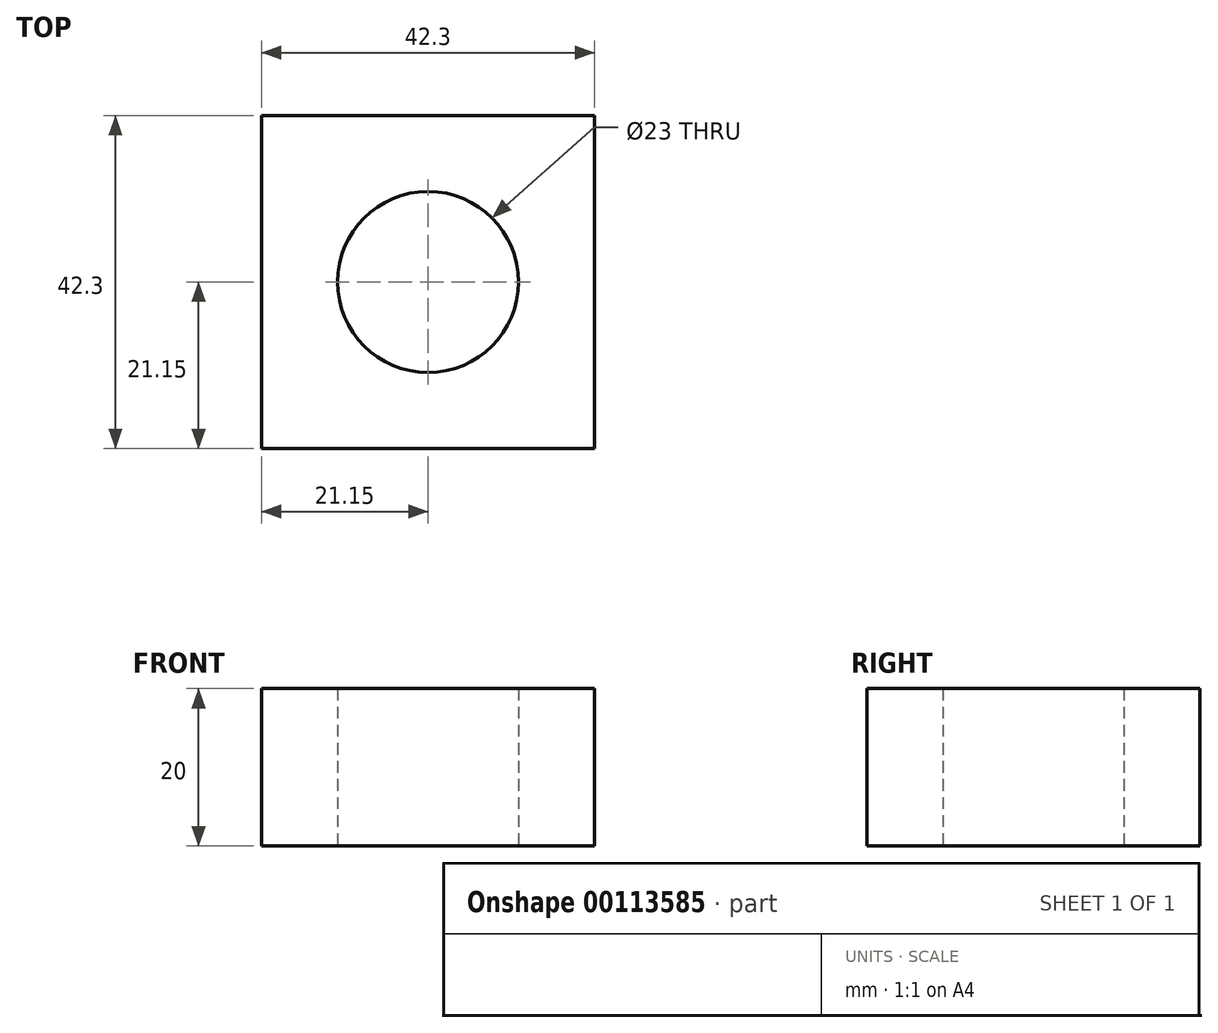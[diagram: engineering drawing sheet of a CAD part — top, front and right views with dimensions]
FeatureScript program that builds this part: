
annotation { "Feature Type Name" : "Feature", "Feature Type Description" : "" }
export const myFeature = defineFeature(function(context is Context, id is Id, definition is map)
    precondition{}
    {
        {
            var Q0;
            Q0=qCreatedBy(makeId("Top.planeOp"),FACE);
            var sketch = newSketch(context, id + "F0", { "sketchPlane" : qUnion([Q0])});
            skLineSegment(sketch, "E0.bottom", {"start": v(0, 0) * mm, "end": v(42.3, 0) * mm});
            skLineSegment(sketch, "E0.top", {"start": v(0, 42.3) * mm, "end": v(42.3, 42.3) * mm});
            skLineSegment(sketch, "E0.left", {"start": v(0, 0) * mm, "end": v(0, 42.3) * mm});
            skLineSegment(sketch, "E0.right", {"start": v(42.3, 0) * mm, "end": v(42.3, 42.3) * mm});
            skCircle(sketch, "E1", {"center": v(21.15, 21.15) * mm, "radius": 11.5 * mm});
            skPoint(sketch, "E1.centerSnap0", {"position": v(0, 21.15) * mm});
            skPoint(sketch, "E1.centerSnap1", {"position": v(21.15, 42.3) * mm});
            skSolve(sketch);
        }
        {
            var Q0;
            Q0=makeQuery(id+"F0.imprint","IMPRINT",FACE,{"disambiguationData":[TD([[makeQuery(id+"F0.imprint","IMPRINT",EDGE,{"derivedFrom":sQuery(id+"F0.wireOp",EDGE,"E0.bottom")}),1.0]])]});
            extrude(context, id + "F1", {"entities" : qUnion([Q0]), "depth" : 20 * mm});
        }
    });
